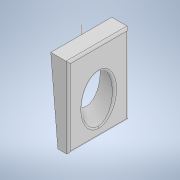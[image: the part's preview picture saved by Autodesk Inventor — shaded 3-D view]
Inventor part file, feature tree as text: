
AUTODESK INVENTOR PART (.ipt)
format: ipt  version: 2021.1 (Build 251245010, 245A)  size: 253,440 bytes
history: native  units: in
note: dims shown in document units (in); Inventor stores cm internally (conversion verified against a paired STEP export)
features: extrude x3, sketch x3, plane x1, fillet x1
ambient origin geometry x8: Origin, YZ Plane, XZ Plane, XY Plane, X Axis, Y Axis, Z Axis, Center Point
bodies: Solid1 (feature_tree)
feature tree (8):
  extrude  "Extrusion1"  Depth=0.5in
  plane  "Work Plane1"
  extrude  "Extrusion2"  Depth=1.75in
  extrude  "Extrusion3"  [1 undecoded]
  fillet  "Fillet3"  Radius=0.9in
  sketch  "Sketch1"  dims[d0=0.0344in d1=0.5in]
  sketch  "Sketch2"  dims[d3=2.3in d4=1.75in]
  sketch  "Sketch3"  dims[d5=0.0in d6=-0.3092in d7=0.9in d8=0.0in d9=0.0in d10=1.0in d12=0.3in d13=0.05in d14=0.0in d16=0.0625in]
note: 1 required parameter value undecoded (feature->parameter linkage not recoverable at this tier; creation-order binding heuristic only, values carry confidence <= 0.55)
